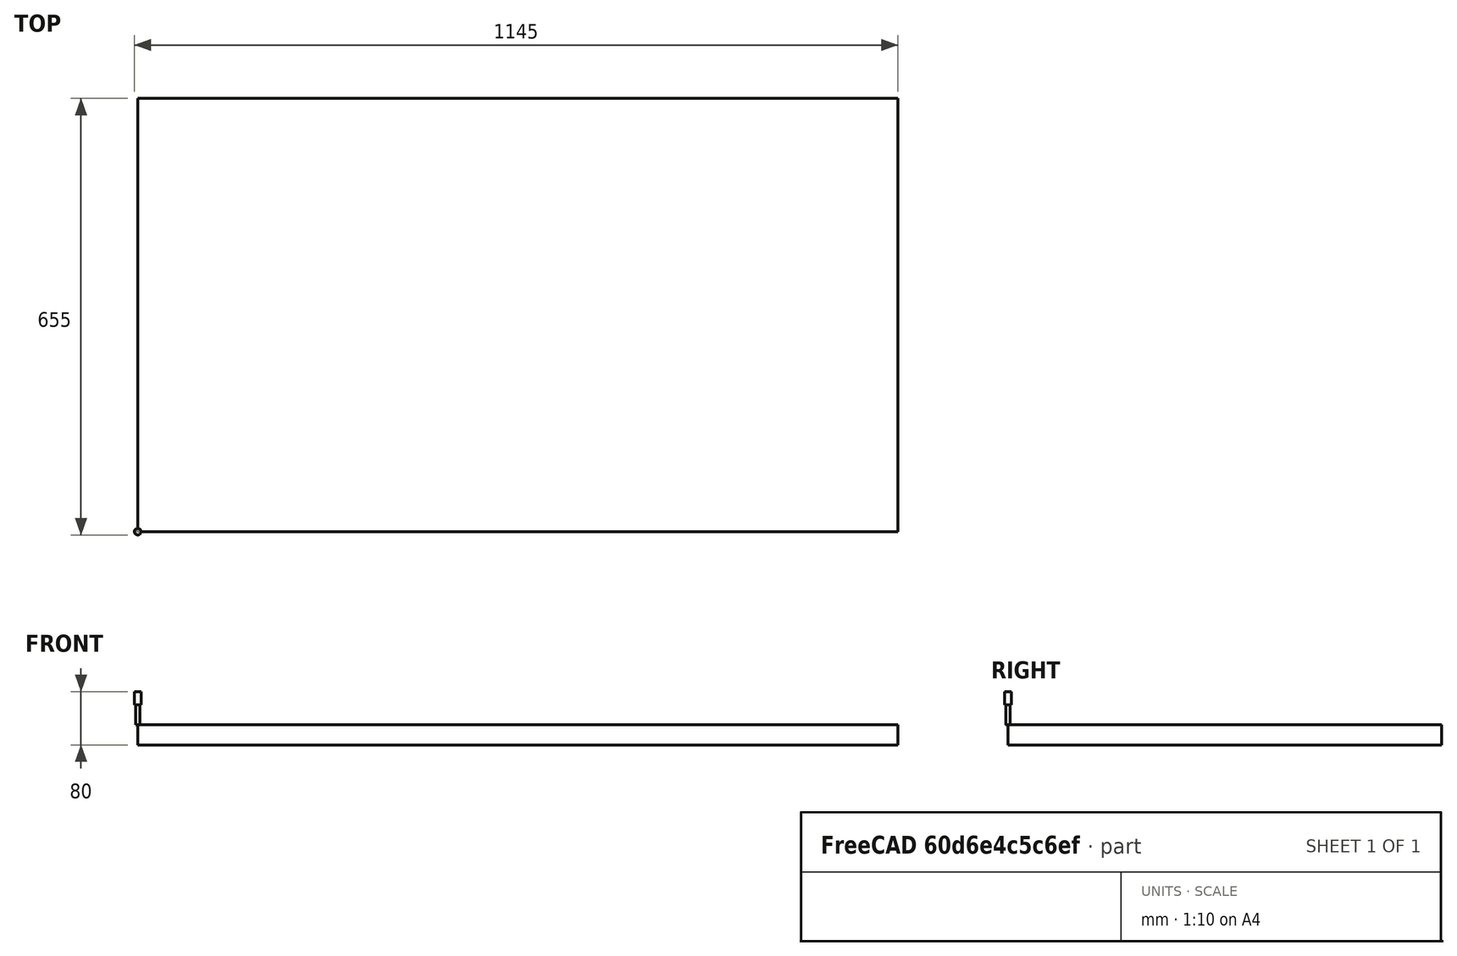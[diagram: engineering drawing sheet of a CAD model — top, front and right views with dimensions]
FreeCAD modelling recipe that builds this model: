
FCSTD DOCUMENT  (FreeCAD 0.19R14555 (Git shallow))
Label: BarrelTableTop
License: All rights reserved
LicenseURL: http://en.wikipedia.org/wiki/All_rights_reserved
objects: Part::FeaturePython×3, Path::FeaturePython×3, App::DocumentObjectGroup×2, Sketcher::SketchObject×1, PartDesign::Pad×1, PartDesign::Body×1, App::FeaturePython×1, Path::FeatureCompoundPython×1, Mesh::FeaturePython×1
note: 8 computed .brp shape members not serialized (recipe doc carries the construction recipe); baked Part::Feature solids carry a one-line shape summary decoded from their .brp

FEATURE [Sketcher::SketchObject] Sketch
  FullyConstrained = true
  MapMode = 5
  Support = -> [XY_Plane]
  sketch-geometry (5):
    g0: LineSegment StartX=0 StartY=650 StartZ=0 EndX=1140 EndY=650 EndZ=0
    g1: LineSegment StartX=1140 StartY=650 StartZ=0 EndX=1140 EndY=0 EndZ=0
    g2: LineSegment StartX=1140 StartY=0 StartZ=0 EndX=0 EndY=0 EndZ=0
    g3: LineSegment StartX=0 StartY=0 StartZ=0 EndX=0 EndY=650 EndZ=0
    g4: Circle CenterX=570 CenterY=325 CenterZ=0 NormalX=0 NormalY=0 NormalZ=1 AngleXU=0 Radius=316.5
  constraints (14):
    c: Coincident(g0,g1)
    c: Coincident(g1,g2)
    c: Coincident(g2,g3)
    c: Coincident(g3,g0)
    c: Horizontal(g0)
    c: Horizontal(g2)
    c: Vertical(g1)
    c: Vertical(g3)
    c: Coincident(g2,g-1)
    c: DistanceX(g2,g2) = 1140  'tlength'
    c: DistanceY(g3,g3) = 650  'twidth'
    c: DistanceX(g2,g4) = 570
    c: DistanceY(g2,g4) = 325
    c: Diameter(g4) = 633
FEATURE [PartDesign::Pad] Pad
  Direction = (1,1,1)
  Length = 30
  Length2 = 100
  Profile = -> Sketch
  Reversed = true
  Type = 0
FEATURE [PartDesign::Body] Body
  Group = -> [Sketch,Pad]
  Origin = -> Origin
  Tip = -> Pad
FEATURE [App::FeaturePython] SetupSheet  # Path/CAM operation (typed FeaturePython)
  ClearanceHeightExpression = OpStockZMax+SetupSheet.ClearanceHeightOffset
  ClearanceHeightOffset = 5
  CoolantMode = 0
  CoolantModes = None | Flood | Mist
  FinalDepthExpression = OpFinalDepth
  HorizRapid = 0
  SafeHeightExpression = OpStockZMax+SetupSheet.SafeHeightOffset
  SafeHeightOffset = 3
  StartDepthExpression = OpStartDepth
  StepDownExpression = OpToolDiameter
  VertRapid = 0
FEATURE [Part::FeaturePython] Clone  label="Model-Body"  # Draft clone (typed FeaturePython)
  AttacherType = Attacher::AttachEngine3D
  Fuse = false
  Objects = -> [Body]
  PathResource = Model
  Scale = (1,1,1)
FEATURE [App::DocumentObjectGroup] Model
  Group = -> [Clone]
FEATURE [Part::FeaturePython] Stock  # WARN: FeaturePython — macro-defined, semantics opaque (R4)
  Height = 30
  Length = 1140
  Placement = pos=(0,0,-30) rot=(0,0,1;0rad)
  StockType = CreateBox
  Width = 650
FEATURE [Part::FeaturePython] ToolBit001  label="6.4mm Endmill"  # Path/CAM toolbit (typed FeaturePython)
  BitPropertyNames = Chipload | CuttingEdgeHeight | Diameter | Flutes | Length | Material | ShankDiameter
  BitShape = /app/freecad/Mod/Path/Tools/Shape/endmill.fcstd
  Chipload = 0
  CuttingEdgeHeight = 30
  Diameter = 6.4
  File = <userpath>/Documents/MensShed/FreeCAD/Bit/6.4mm_Endmill.fctb
  Flutes = 0
  Length = 50
  Material = 0
  ShankDiameter = 10
  ShapeName = endmill
FEATURE [Path::FeaturePython] __4mm_Endmill  label="6.4mm Endmill001"  # Path/CAM operation (typed FeaturePython)
  HorizFeed = 40
  HorizRapid = 0
  SpindleDir = 0
  SpindleSpeed = 10000
  Tool = -> ToolBit001
  ToolNumber = 2
  VertFeed = 40
  VertRapid = 0
  expr: HorizRapid = SetupSheet.HorizRapid
  expr: VertRapid = SetupSheet.VertRapid
FEATURE [App::DocumentObjectGroup] Tools
  Group = -> [__4mm_Endmill]
FEATURE [Path::FeaturePython] Profile  # Path/CAM operation (typed FeaturePython)
  Active = true
  AreaParams:
    Tolerance = 1e-07
    FitArcs = True
    Simplify = False
    CleanDistance = 0.0
    Accuracy = 0.01
    Unit = 1.0
    MinArcPoints = 4
    MaxArcPoints = 100
    ClipperScale = 10000000.0
    Fill = 0
    Coplanar = 0
    Reorient = True
    Outline = False
    Explode = False
    OpenMode = 0
    Deflection = 0.01
    SubjectFill = 0
    ClipFill = 0
    Offset = -3.2
    ExtraPass = 0
    Stepover = 0.0
    LastStepover = 0.0
    JoinType = 0
    EndType = 0
    MiterLimit = 2.0
    RoundPrecision = 0.0
    PocketMode = 0
    ToolRadius = 1.0
    PocketExtraOffset = 0.0
    PocketStepover = 0.0
    PocketLastStepover = 0.0
    FromCenter = False
    Angle = 45.0
    AngleShift = 0.0
    Shift = 0.0
    Thicken = False
    SectionCount = -1
    Stepdown = 1.0
    SectionOffset = 0.0
    SectionTolerance = 1e-06
    SectionMode = 2
    Project = False
  AttemptInverseAngle = true
  Base = -> [Clone]
  ClearanceHeight = 5
  CoolantMode = None
  CycleTime = 00:01:32
  Direction = 0
  EnableRotation = 0
  FinalDepth = -8
  HandleMultipleFeatures = 0
  InverseAngle = false
  JoinType = 0
  LimitDepthToFace = true
  MiterLimit = 0.1
  OffsetExtra = 0
  OpFinalDepth = -30
  OpStartDepth = 0
  OpStockZMax = 0
  OpStockZMin = -30
  OpToolDiameter = 6.4
  PathParams = {'orientation': 1, 'feedrate': 40.0, 'feedrate_v': 40.0, 'verbose': True, 'resume_height': 3.0, 'retraction': 5.0, 'return_end': True, 'preamble': False}
  ReverseDirection = false
  SafeHeight = 3
  Side = 1
  StartDepth = 0
  StartPoint = (0,0,0)
  StepDown = 6.4
  ToolController = -> __4mm_Endmill
  UseComp = true
  UseStartPoint = false
  processCircles = false
  processHoles = false
  processPerimeter = true
  expr: ClearanceHeight = OpStockZMax + SetupSheet.ClearanceHeightOffset
  expr: SafeHeight = OpStockZMax + SetupSheet.SafeHeightOffset
  expr: StepDown = OpToolDiameter
  expr: FinalDepth = -8
  expr: StartDepth = 0
FEATURE [Path::FeatureCompoundPython] Operations  # Path/CAM operation (typed FeaturePython)
  Group = -> [Profile]
  UsePlacements = false
FEATURE [Path::FeaturePython] Job  # Path/CAM operation (typed FeaturePython)
  CycleTime = 00:01:32
  Fixtures = G54
  GeometryTolerance = 0.01
  LastPostProcessDate = 2022-01-19 13:48:43.297075
  LastPostProcessOutput = <userpath>/Documents/MensShed/BarrelTableTop.ngc
  Model = -> Model
  Operations = -> Operations
  OrderOutputBy = 0
  PostProcessor = 7
  PostProcessorOutputFile = <userpath>/Documents/MensShed/BarrelTableTop.ngc
  SetupSheet = -> SetupSheet
  SplitOutput = false
  Stock = -> Stock
  Tools = -> Tools
FEATURE [Mesh::FeaturePython] CutMaterial  # WARN: FeaturePython — macro-defined, semantics opaque (R4)
